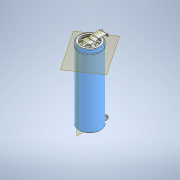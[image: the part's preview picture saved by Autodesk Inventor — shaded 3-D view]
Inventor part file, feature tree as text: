
AUTODESK INVENTOR PART (.ipt)
format: ipt  version: 2020 (Build 240168000, 168)  size: 627,200 bytes
history: native  units: mm
features: sketch x6, plane x4, extrude x3, fillet x3, revolve x1, other x1
ambient origin geometry x8: Origin, YZ Plane, XZ Plane, XY Plane, X Axis, Y Axis, Z Axis, Center Point
bodies: Solid1 (feature_tree), Solid2 (feature_tree), Body1 (feature_tree), Body2 (feature_tree)
feature tree (18):
  extrude  "Extrusion1"  Depth=10.0mm TaperAngle=0.0deg
  plane  "Work Plane3"
  extrude  "Extrusion2"  [1 undecoded]
  plane  "Work Plane4"
  revolve  "Revolution1"  [1 undecoded]
  fillet  "Fillet1"  [1 undecoded]
  extrude  "Extrusion3"  Depth=1.0mm
  fillet  "Fillet2"  Radius=1.0mm
  fillet  "Fillet4"  Radius=0.12mm
  sketch  "Sketch5"  dims[d16=0.12mm]
  plane  "Work Plane2"
  sketch  "Sketch2"  dims[d4=-3.0mm d5=-4.0mm]
  sketch  "Sketch1"  dims[d0=2.0mm d1=0.0mm d2=10.0mm d3=0.0mm]
  plane  "Work Plane1"
  sketch  "Sketch3"  dims[d6=19.4mm d7=1.0mm d8=0.0mm d9=90.0deg]
  other  "Work Axis1"
  sketch  "Sketch4"  dims[d10=0.1mm d11=0.12mm d13=1.0mm d14=0.12mm]
  sketch  "Sketch6"  dims[d17=3.0mm d18=3.6mm d19=7.0mm d20=0.0mm d21=2.0mm d26=3.2mm d27=1.6mm d28=9.0mm d29=1.0mm]
note: 3 required parameter values undecoded (feature->parameter linkage not recoverable at this tier; creation-order binding heuristic only, values carry confidence <= 0.55)